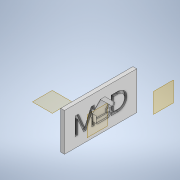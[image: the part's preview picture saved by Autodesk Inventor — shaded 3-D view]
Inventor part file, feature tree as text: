
AUTODESK INVENTOR PART (.ipt)
format: ipt  version: 2020.4 (Build 244396000, 396)  size: 295,424 bytes
history: native  units: in
note: dims shown in document units (in); Inventor stores cm internally (conversion verified against a paired STEP export)
features: extrude x8, plane x5, sketch x4
ambient origin geometry x8: Origin, YZ Plane, XZ Plane, XY Plane, X Axis, Y Axis, Z Axis, Center Point
bodies: Solid1 (feature_tree)
feature tree (17):
  plane  "Work Plane7"
  extrude  "Extrusion2"  Depth=0.1654in
  plane  "Work Plane5"
  extrude  "Extrusion3"  Depth=0.1575in TaperAngle=0.0deg
  plane  "Work Plane4"
  extrude  "Extrusion4"  Depth=0.0709in
  plane  "Work Plane3"
  sketch  "Sketch6"  dims[d117=0.0709in d118=0.0709in]
  extrude  "Extrusion6"  Depth=0.0394in
  plane  "Work Plane6"
  extrude  "Extrusion10"  Depth=0.7756in
  extrude  "Extrusion13"  Depth=0.0394in
  extrude  "Extrusion14"  Depth=0.0394in
  extrude  "Extrusion15"  Depth=0.0394in
  sketch  "Sketch4"  dims[d42=3.1496in d43=0.1654in]
  sketch  "Sketch5"  dims[d45=1.4961in d46=0.0in d47=0.1575in d48=0.0in]
  sketch  "Sketch8"  dims[d119=0.0984in d120=0.0984in d124=0.7756in d136=0.0653in d137=0.0653in d143=0.5961in d144=0.5961in d147=0.1307in d161=0.1063in d180=0.1063in d185=0.1601in d186=0.1601in d237=0.1102in d238=0.0in d259=0.1063in d262=0.1063in d263=0.1063in d267=0.7368in d269=0.1921in d274=0.2815in d276=0.1921in d279=0.1102in d280=0.0in d311=0.1457in d316=0.1457in d366=0.4921in d389=0.1417in d390=0.1417in d406=0.0803in d434=0.1228in d442=0.4247in d445=0.1102in d446=0.0in d447=0.1417in d448=0.8661in d455=0.1102in d456=0.0in d461=0.0709in d462=0.0in d463=0.0472in d464=0.0in d465=0.0236in d466=0.0in d468=3.185in d33=0.0394in d34=0.0394in d35=0.0394in d36=0.0059in d37=0.0098in d38=0.0148in d39=0.5635in d40=0.0295in d41=0.8108in d44=0.0148in d443=0.0197in d444=0.0344in d449=0.0197in d450=0.0344in d451=0.0197in d452=0.0344in d453=0.0197in d454=0.0344in d457=0.0197in d458=0.0344in d459=0.0197in d460=0.0344in]
